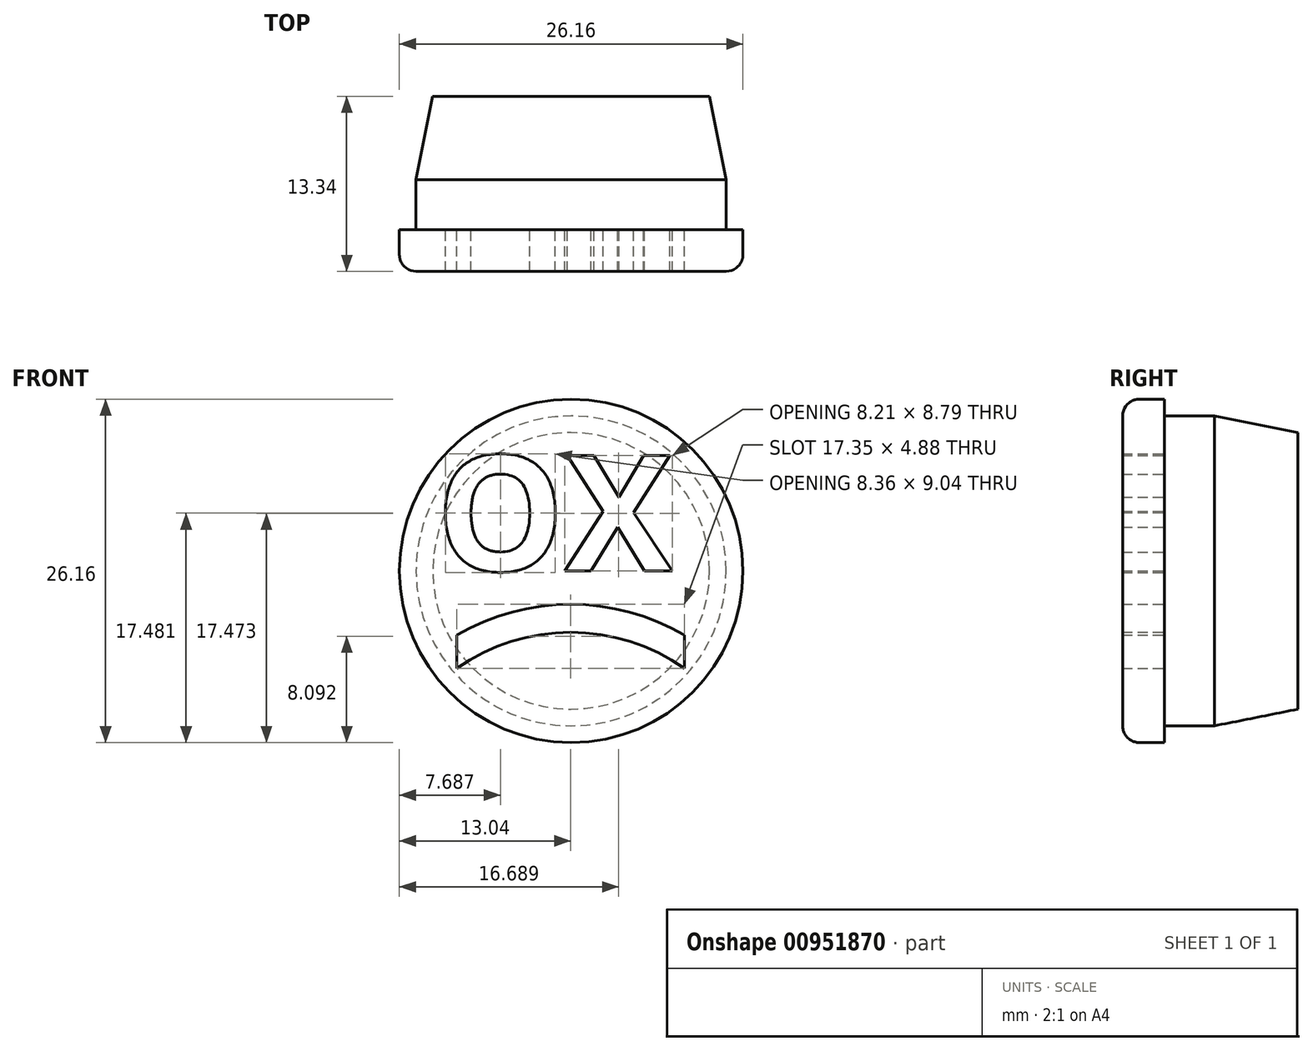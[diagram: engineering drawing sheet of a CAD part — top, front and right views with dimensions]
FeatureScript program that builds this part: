
annotation { "Feature Type Name" : "Feature", "Feature Type Description" : "" }
export const myFeature = defineFeature(function(context is Context, id is Id, definition is map)
    precondition{}
    {
        {
            var Q0;
            Q0=qCreatedBy(makeId("Front.planeOp"),FACE);
            var sketch = newSketch(context, id + "F0", { "sketchPlane" : qUnion([Q0])});
            skCircle(sketch, "E0", {"center": v(0, 0) * mm, "radius": 11.81 * mm});
            skCircle(sketch, "E1", {"center": v(0, 0) * mm, "radius": 13.08 * mm});
            skText(sketch, "E2", { "text": "OX", "fontName": "OpenSans-Bold.ttf"});
            skLineSegment(sketch, "E3", {"start": v(8.64, -4.9) * mm, "end": v(8.64, -7.43) * mm});
            skLineSegment(sketch, "E4", {"start": v(-8.72, -4.9) * mm, "end": v(-8.72, -7.43) * mm});
            skArc(sketch, "E5", {"start": v(8.64, -7.43) * mm, "mid": v(-0.04, -4.68) * mm, "end": v(-8.72, -7.43) * mm});
            skArc(sketch, "E6.0", {"start": v(8.64, -4.9) * mm, "mid": v(-0.04, -2.55) * mm, "end": v(-8.72, -4.9) * mm});
            skLineSegment(sketch, "E7", {"start": v(-8.72, -7.43) * mm, "end": v(-8.72, -4.9) * mm});
            skLineSegment(sketch, "E8", {"start": v(8.64, -7.43) * mm, "end": v(8.64, -4.9) * mm});
            const initialGuessF0  = {"E2": [-0.01029, 0, 1, 0, 0.00886]};
            skSetInitialGuess(sketch, initialGuessF0);
            skSolve(sketch);
        }
        {
            var Q0;
            Q0=makeQuery(id+"F0.imprint","IMPRINT",FACE,{"disambiguationData":[TD([[makeQuery(id+"F0.imprint","IMPRINT",EDGE,{"derivedFrom":sQuery(id+"F0.wireOp",EDGE,"E2.sketch_text.stroke-8")}),1.0]])]});
            var Q1;
            Q1=makeQuery(id+"F0.imprint","IMPRINT",FACE,{"disambiguationData":[TD([[makeQuery(id+"F0.imprint","IMPRINT",EDGE,{"derivedFrom":sQuery(id+"F0.wireOp",EDGE,"E0")}),1.0]])]});
            var Q2;
            Q2=makeQuery(id+"F0.imprint","IMPRINT",FACE,{"disambiguationData":[TD([[makeQuery(id+"F0.imprint","IMPRINT",EDGE,{"derivedFrom":sQuery(id+"F0.wireOp",EDGE,"E0")}),-1.0]])]});
            extrude(context, id + "F1", {"entities" : qUnion([Q0, Q1, Q2]), "depth" : 3.17 * mm, "offsetDistance" : 25.4 * mm});
        }
        {
            var Q0;
            Q0=makeQuery(id+"F0.imprint","IMPRINT",FACE,{"disambiguationData":[TD([[makeQuery(id+"F0.imprint","IMPRINT",EDGE,{"derivedFrom":sQuery(id+"F0.wireOp",EDGE,"E0")}),1.0]])]});
            var Q1;
            Q1=makeQuery(id+"F0.imprint","IMPRINT",FACE,{"disambiguationData":[TD([[makeQuery(id+"F0.imprint","IMPRINT",EDGE,{"derivedFrom":sQuery(id+"F0.wireOp",EDGE,"E5")}),-1.0]])]});
            var Q2;
            Q2=makeQuery(id+"F0.imprint","IMPRINT",FACE,{"disambiguationData":[TD([[makeQuery(id+"F0.imprint","IMPRINT",EDGE,{"derivedFrom":sQuery(id+"F0.wireOp",EDGE,"E2.sketch_text.stroke-14")}),-1.0]])]});
            var Q3;
            Q3=makeQuery(id+"F0.imprint","IMPRINT",FACE,{"disambiguationData":[TD([[makeQuery(id+"F0.imprint","IMPRINT",EDGE,{"derivedFrom":sQuery(id+"F0.wireOp",EDGE,"E2.sketch_text.stroke-8")}),1.0]])]});
            var Q4;
            Q4=makeQuery(id+"F0.imprint","IMPRINT",FACE,{"disambiguationData":[TD([[makeQuery(id+"F0.imprint","IMPRINT",EDGE,{"derivedFrom":sQuery(id+"F0.wireOp",EDGE,"E2.sketch_text.stroke-0")}),-1.0]])]});
            extrude(context, id + "F2", {"entities" : qUnion([Q0, Q1, Q2, Q3, Q4]), "oppositeDirection" : true, "depth" : 10.16 * mm, "offsetDistance" : 25.4 * mm});
        }
        {
            var Q0;
            Q0=makeQuery(id+"F1.opExtrude","CAP_EDGE",EDGE,{"disambiguationData":[OSD([sQuery(id+"F0.wireOp",EDGE,"E1")])],"isStart":false});
            fillet(context, id + "F3", {"entities" : qUnion([Q0]), "radius" : 1.27 * mm, "tangentPropagation" : true, "allowEdgeOverflow" : false});
        }
        {
            var Q0;
            Q0=makeQuery(id+"F2.opExtrude","CAP_EDGE",EDGE,{"disambiguationData":[OSD([sQuery(id+"F0.wireOp",EDGE,"E0")])],"isStart":false});
            chamfer(context, id + "F4", {"entities" : qUnion([Q0]), "chamferType" : ChamferType.TWO_OFFSETS, "width1" : 6.35 * mm, "oppositeDirection" : false, "width2" : 1.27 * mm, "tangentPropagation" : true});
        }
    });
